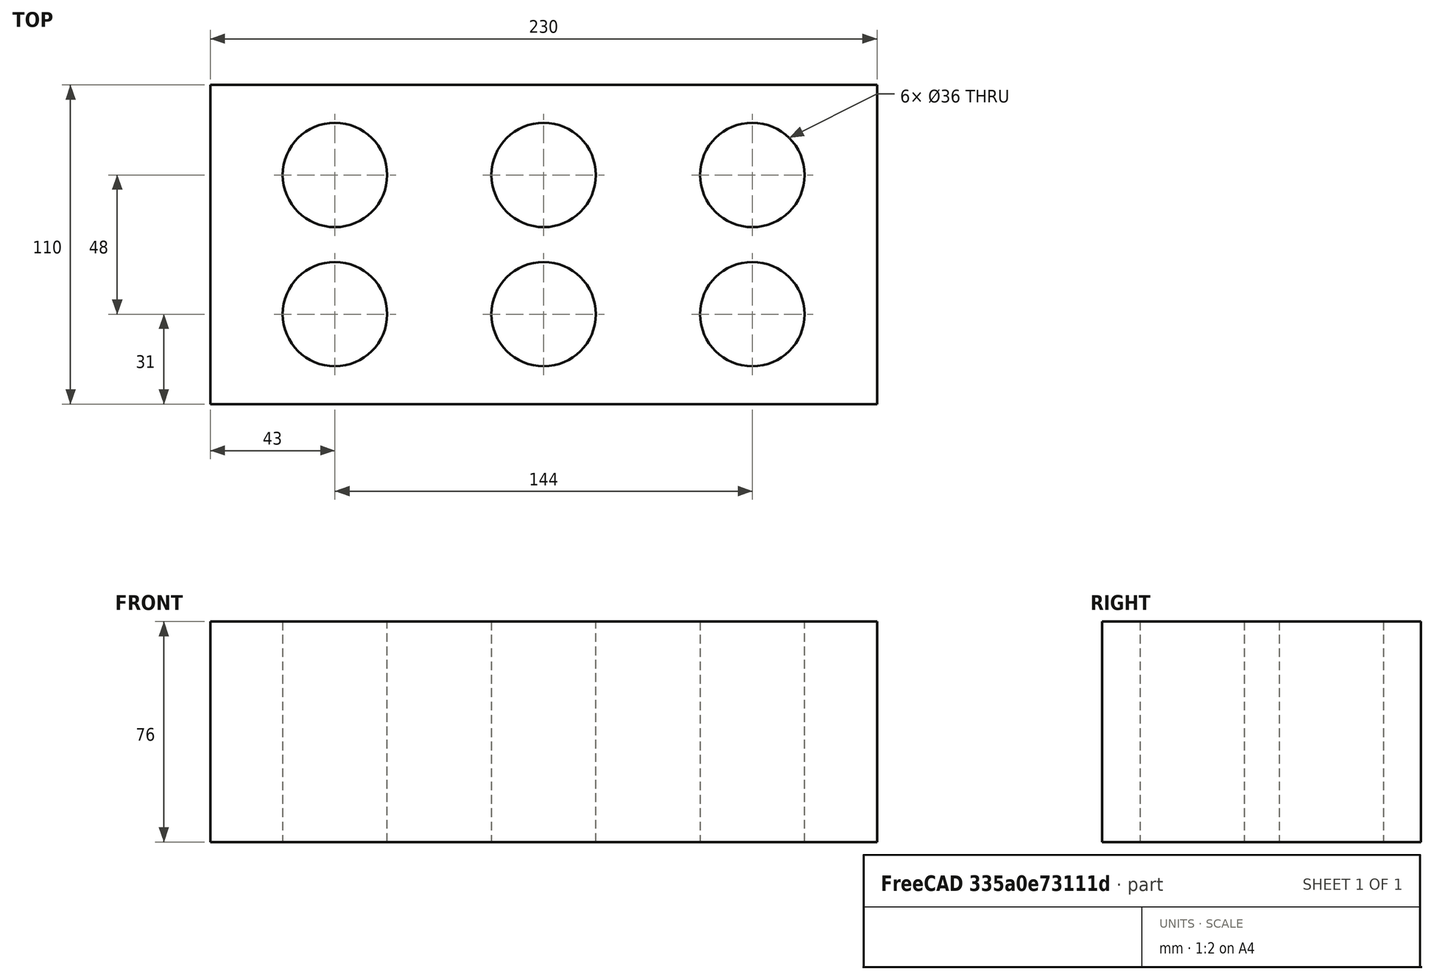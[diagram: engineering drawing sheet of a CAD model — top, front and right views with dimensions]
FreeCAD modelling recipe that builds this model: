
FCSTD DOCUMENT  (FreeCAD 0.21R33694 (Git))
Label: OJT1_T09R01-lego
License: All rights reserved
LicenseURL: http://en.wikipedia.org/wiki/All_rights_reserved
objects: Part::Cylinder×6, Part::Cut×6, Part::Box×1
note: 13 computed .brp shape members not serialized (recipe doc carries the construction recipe); baked Part::Feature solids carry a one-line shape summary decoded from their .brp

FEATURE [Part::Box] Box  label="Cub"
  AttacherType = Attacher::AttachEngine3D
  Height = 76
  Length = 230
  Placement = pos=(-43,-31,0) rot=(0,0,1;0rad)
  Width = 110
FEATURE [Part::Cylinder] Cylinder  label="Cilindre"
  Angle = 360
  AttacherType = Attacher::AttachEngine3D
  FirstAngle = 0
  Height = 76
  Placement = pos=(72,0,0) rot=(0,0,1;0rad)
  Radius = 18
  SecondAngle = 0
FEATURE [Part::Cylinder] Cylinder001  label="Cilindre001"
  Angle = 360
  AttacherType = Attacher::AttachEngine3D
  FirstAngle = 0
  Height = 76
  Placement = pos=(144,0,0) rot=(0,0,1;0rad)
  Radius = 18
  SecondAngle = 0
FEATURE [Part::Cylinder] Cylinder002  label="Cilindre002"
  Angle = 360
  AttacherType = Attacher::AttachEngine3D
  FirstAngle = 0
  Height = 76
  Placement = pos=(0,48,0) rot=(0,0,1;0rad)
  Radius = 18
  SecondAngle = 0
FEATURE [Part::Cylinder] Cylinder003  label="Cilindre003"
  Angle = 360
  AttacherType = Attacher::AttachEngine3D
  FirstAngle = 0
  Height = 76
  Placement = pos=(72,48,0) rot=(0,0,1;0rad)
  Radius = 18
  SecondAngle = 0
FEATURE [Part::Cylinder] Cylinder004  label="Cilindre004"
  Angle = 360
  AttacherType = Attacher::AttachEngine3D
  FirstAngle = 0
  Height = 76
  Placement = pos=(144,48,0) rot=(0,0,1;0rad)
  Radius = 18
  SecondAngle = 0
FEATURE [Part::Cylinder] Cylinder005  label="Cilindre005"
  Angle = 360
  AttacherType = Attacher::AttachEngine3D
  FirstAngle = 0
  Height = 76
  Radius = 18
  SecondAngle = 0
FEATURE [Part::Cut] Cut
  Base = -> Box
  Refine = true
  Tool = -> Cylinder
FEATURE [Part::Cut] Cut001
  Base = -> Cut
  Refine = true
  Tool = -> Cylinder005
FEATURE [Part::Cut] Cut002
  Base = -> Cut001
  Refine = true
  Tool = -> Cylinder004
FEATURE [Part::Cut] Cut003
  Base = -> Cut002
  Refine = true
  Tool = -> Cylinder003
FEATURE [Part::Cut] Cut004
  Base = -> Cut003
  Refine = true
  Tool = -> Cylinder002
FEATURE [Part::Cut] Cut005
  Base = -> Cut004
  Refine = true
  Tool = -> Cylinder001
